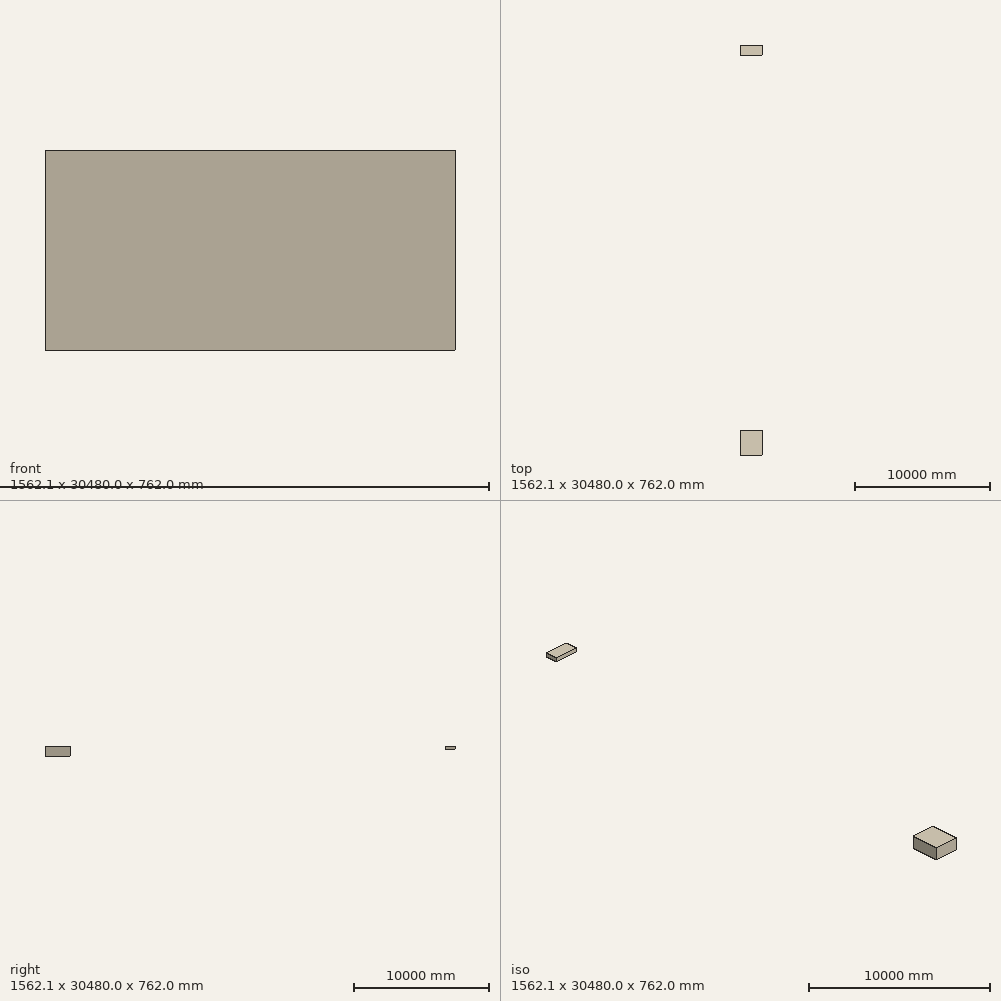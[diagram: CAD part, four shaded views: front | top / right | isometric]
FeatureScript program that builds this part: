
annotation { "Feature Type Name" : "Feature", "Feature Type Description" : "" }
export const myFeature = defineFeature(function(context is Context, id is Id, definition is map)
    precondition{}
    {
        {
            var Q0;
            Q0=qCreatedBy(makeId("Right.planeOp"),FACE);
            var sketch = newSketch(context, id + "F0", { "sketchPlane" : qUnion([Q0])});
            skLineSegment(sketch, "E0", {"start": v(0, 0) * mm, "end": v(-30480, 0) * mm, "construction": true});
            skSolve(sketch);
        }
        {
            var Q0;
            Q0=qCreatedBy(makeId("Top.planeOp"),FACE);
            var sketch = newSketch(context, id + "F1", { "sketchPlane" : qUnion([Q0])});
            skLineSegment(sketch, "E1.bottom", {"start": v(-781.05, -30480) * mm, "end": v(781.05, -30480) * mm});
            skLineSegment(sketch, "E1.top", {"start": v(-781.05, -28651.2) * mm, "end": v(781.05, -28651.2) * mm});
            skLineSegment(sketch, "E1.left", {"start": v(-781.05, -30480) * mm, "end": v(-781.05, -28651.2) * mm});
            skLineSegment(sketch, "E1.right", {"start": v(781.05, -30480) * mm, "end": v(781.05, -28651.2) * mm});
            skSolve(sketch);
        }
        {
            var Q0;
            Q0 = qSketchRegion(id + "F1", true);
            extrude(context, id + "F2", {"entities" : qUnion([Q0]), "oppositeDirection" : true, "depth" : 762 * mm, "offsetDistance" : 25.4 * mm});
        }
        {
            var Q0;
            Q0=qCreatedBy(makeId("Top.planeOp"),FACE);
            var sketch = newSketch(context, id + "F3", { "sketchPlane" : qUnion([Q0])});
            skLineSegment(sketch, "E2.bottom", {"start": v(-781.05, 0) * mm, "end": v(781.05, 0) * mm});
            skLineSegment(sketch, "E2.top", {"start": v(-781.05, -762) * mm, "end": v(781.05, -762) * mm});
            skLineSegment(sketch, "E2.left", {"start": v(-781.05, 0) * mm, "end": v(-781.05, -762) * mm});
            skLineSegment(sketch, "E2.right", {"start": v(781.05, 0) * mm, "end": v(781.05, -762) * mm});
            skSolve(sketch);
        }
        {
            var Q0;
            Q0 = qSketchRegion(id + "F3", true);
            extrude(context, id + "F4", {"entities" : qUnion([Q0]), "oppositeDirection" : true, "depth" : 254 * mm, "offsetDistance" : 25.4 * mm});
        }
    });
